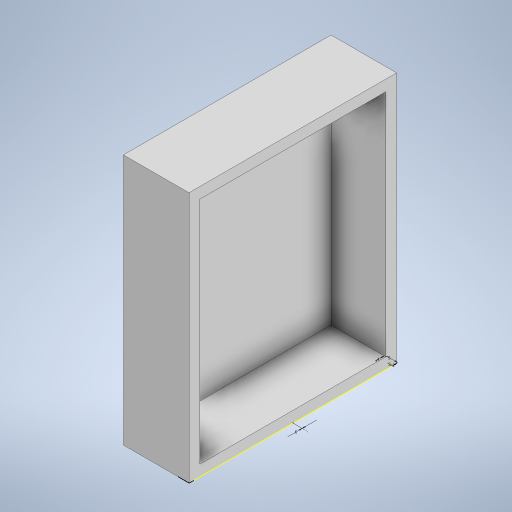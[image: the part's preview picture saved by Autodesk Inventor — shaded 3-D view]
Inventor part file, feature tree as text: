
AUTODESK INVENTOR PART (.ipt)
format: ipt  version: 2024.3 (Build 283343000, 343)  size: 220,160 bytes
history: native  units: mm
features: sketch x2, extrude x2, other x1
ambient origin geometry x8: Origin, YZ Plane, XZ Plane, XY Plane, X Axis, Y Axis, Z Axis, Center Point
bodies: Body1 (feature_tree)
feature tree (5):
  other  "Sólido1"
  sketch  "Boceto1"  dims[d0=85.0mm d1=105.0mm]
  extrude  "Extrusión1"  Depth=105.0mm
  extrude  "Extrusión2"  Depth=5.0mm
  sketch  "Boceto2"  dims[d2=5.0mm d3=5.0mm d4=5.0mm d5=5.0mm d6=30.0mm d7=0.0mm d8=5.0mm d9=0.0mm d10=2.0mm d11=2.0mm d12=4.0mm d13=5.0mm d14=0.0mm]
